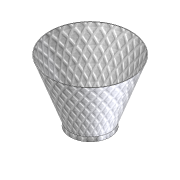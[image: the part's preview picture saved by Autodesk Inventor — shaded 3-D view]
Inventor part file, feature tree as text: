
AUTODESK INVENTOR PART (.ipt)
format: ipt  version: 2012 (Build 160160000, 160)  size: 108,544 bytes
history: native  units: in
note: dims shown in document units (in); Inventor stores cm internally (conversion verified against a paired STEP export)
features: revolve x1, sketch x1
ambient origin geometry x8: Origin, YZ Plane, XZ Plane, XY Plane, X Axis, Y Axis, Z Axis, Center Point
bodies: Solid1 (feature_tree)
feature tree (2):
  revolve  "Revolution1"  [1 undecoded]
  sketch  "Sketch1"  dims[d0=14.25in d1=1.0in d2=0.0in d3=9.3125in d4=0.125in d5=4.5in d6=90.0deg]
note: 1 required parameter value undecoded (feature->parameter linkage not recoverable at this tier; creation-order binding heuristic only, values carry confidence <= 0.55)
